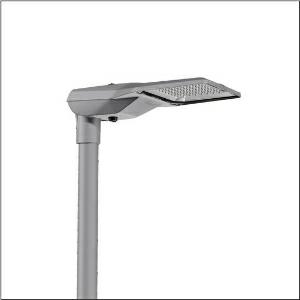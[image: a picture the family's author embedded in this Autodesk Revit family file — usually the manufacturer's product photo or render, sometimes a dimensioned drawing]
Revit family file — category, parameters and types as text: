
# Revit family: streetlight_sl_21_iq_midi___st1_0a_5xe3d31y08nb_4ee3
name_source: partatom
category: Lighting Fixtures
units: mm (PartAtom-declared; Revit-internal decimal feet)

## family parameters
Cut with Voids When Loaded = No
Host = Face
Light Source = No
Part Type = Normal
Room Calculation Point = No
Round Connector Dimension = Use Diameter
Shared = No

## types (1)
- --- (1 x LED, 21550 lm, 136.6 W, 3000K)
    Apparent Load = 137 VA
    CIE Flux Codes = 40 73 97 100 100
    Color Rendering = 70
    Color Temperature = 3000K
    Default Elevation = 1800 mm
    Description = Streetlight SL 21 iQ midi, mast luminaire, primary light control with lens, of PMMA, primary optical cover: cover, of toughened safety glass, transparent, light distribution: ST1.0a, light emission: direct distribution, primary light characteristic: asymmetric, installation type: post-top, side-entry, LED, High Power LED, rated luminous flux: 21.550lm, luminous efficacy: 158lm/W, light colour: 730, colour temperature: 3000K, control gear: iQ-Street Remote, D4i with power reduction, control: pre-setting: logarithmic dimming characteristic, Street-Remote, Auto-Match, Temp-Guard, Lumen-Switch, Night-Set, Smart-Wire, Light-Fading, Desk-Remote (wireless, voltage-free reading and setting of iQ features in the workshop via application-optimized NFC function/RFID function), optimised constant luminous flux control (CLO 2.0), mains connection: 230..240V, AC, 50/60Hz, start of lifetime: 137W, end of service life: 144W, reduction: 61W, luminaire housing, of diecast aluminium, powder-coated, SITECO metallic grey (DB 702S), corrosivity category C5 high according to DIN EN ISO 12944, please order mast flange separately, inclination adjustable: 0°, 5°, 10°, 15°, sealing non-destructively replaceable, multi-level sealing system, length: 644mm, width: 335mm, height: 110mm, mast flange for spigot size: 42mm (side-entry): 5XC10008XM4, 60/48mm (side-entry/post-top): 5XC10108XM2, 76/60mm (side-entry/post-top): 5XC10108XM1, mounting height: 4..8m, Smart Interface below and above, protection rating (complete): IP66, insulation class (complete): insulation class II (safety insulation), certification: CE, ENEC, ENEC+, VDE, impact resistance: IK10, permissible operating ambient temperature for outdoor applications: -40..+50°C, standard-compliant lighting for roads and squares, packaging unit: 1 piece

Light Distribution: ST1.0a
    Height = 111 mm
    Lamp = 1 x LED
    Lamp Light Flux = 21550 lm
    Lamp Power = 136.6 W
    Lamp count = 1
    Length = 644 mm
    Luminous efficacy = 158 lm/W
    Manufacturer = Siteco
    ModVariant = No
    Model = 5XE3D31Y08NB
    Number of Poles = 1
    OnlyDefault = Yes
    Power Factor = 1
    Product Name = Streetlight SL 21 iQ midi | ST1.0a
    Product group = mast luminaire | pylon top
    ProductGroupID = 6100
    Protection Class = Protection class II
    Protection Degree = IP 66
    RLX_Detail_Level = 1
    RLX_Emergency_Light_Flux = 0 lm
    RLX_Emergency_Type = 0
    RLX_Emergency_Type_DB = No
    RlxData = <blob elided: 91441 chars, md5=ce96e6bc>
    Socket = socket
    Standby Power = 0 W
    System Light Flux = 21550 lm
    System Power = 137 W
    Type Comments = factory setting: luminous flux: 100 % | dim-lin: 254 | 733 mA
    Type Image = l_1004304.jpg
    URL = http://relux.com
    VarID = @adj_113929
    Voltage = 0 V
    Weight = 0.00 kg
    Width = 336 mm

## geometry (parser evidence)
native form markers: Blend x4, Sweep x11
no freeform markers — native parametric forms only
